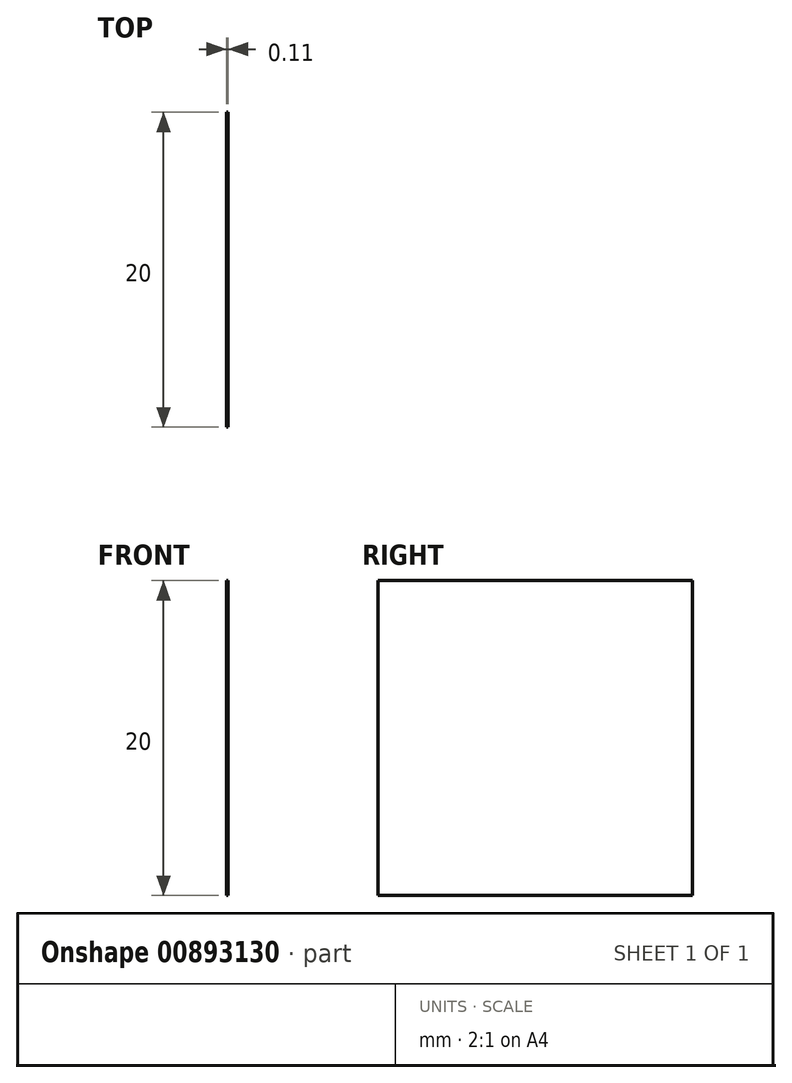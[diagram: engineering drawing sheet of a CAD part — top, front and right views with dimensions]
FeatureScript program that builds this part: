
annotation { "Feature Type Name" : "Feature", "Feature Type Description" : "" }
export const myFeature = defineFeature(function(context is Context, id is Id, definition is map)
    precondition{}
    {
        {
            var Q0;
            Q0=qCreatedBy(makeId("Right.planeOp"),FACE);
            var sketch = newSketch(context, id + "F0", { "sketchPlane" : qUnion([Q0])});
            skLineSegment(sketch, "E0.bottom", {"start": v(0, 0) * mm, "end": v(20, 0) * mm});
            skLineSegment(sketch, "E0.top", {"start": v(0, -20) * mm, "end": v(20, -20) * mm});
            skLineSegment(sketch, "E0.left", {"start": v(0, 0) * mm, "end": v(0, -20) * mm});
            skLineSegment(sketch, "E0.right", {"start": v(20, 0) * mm, "end": v(20, -20) * mm});
            skSolve(sketch);
        }
        {
            var Q0;
            Q0=makeQuery(id+"F0.imprint","IMPRINT",FACE,{"disambiguationData":[TD([[makeQuery(id+"F0.imprint","IMPRINT",EDGE,{"derivedFrom":sQuery(id+"F0.wireOp",EDGE,"E0.bottom")}),-1.0]])]});
            extrude(context, id + "F1", {"entities" : qUnion([Q0]), "depth" : .10718 * mm, "offsetDistance" : 25 * mm});
        }
    });
